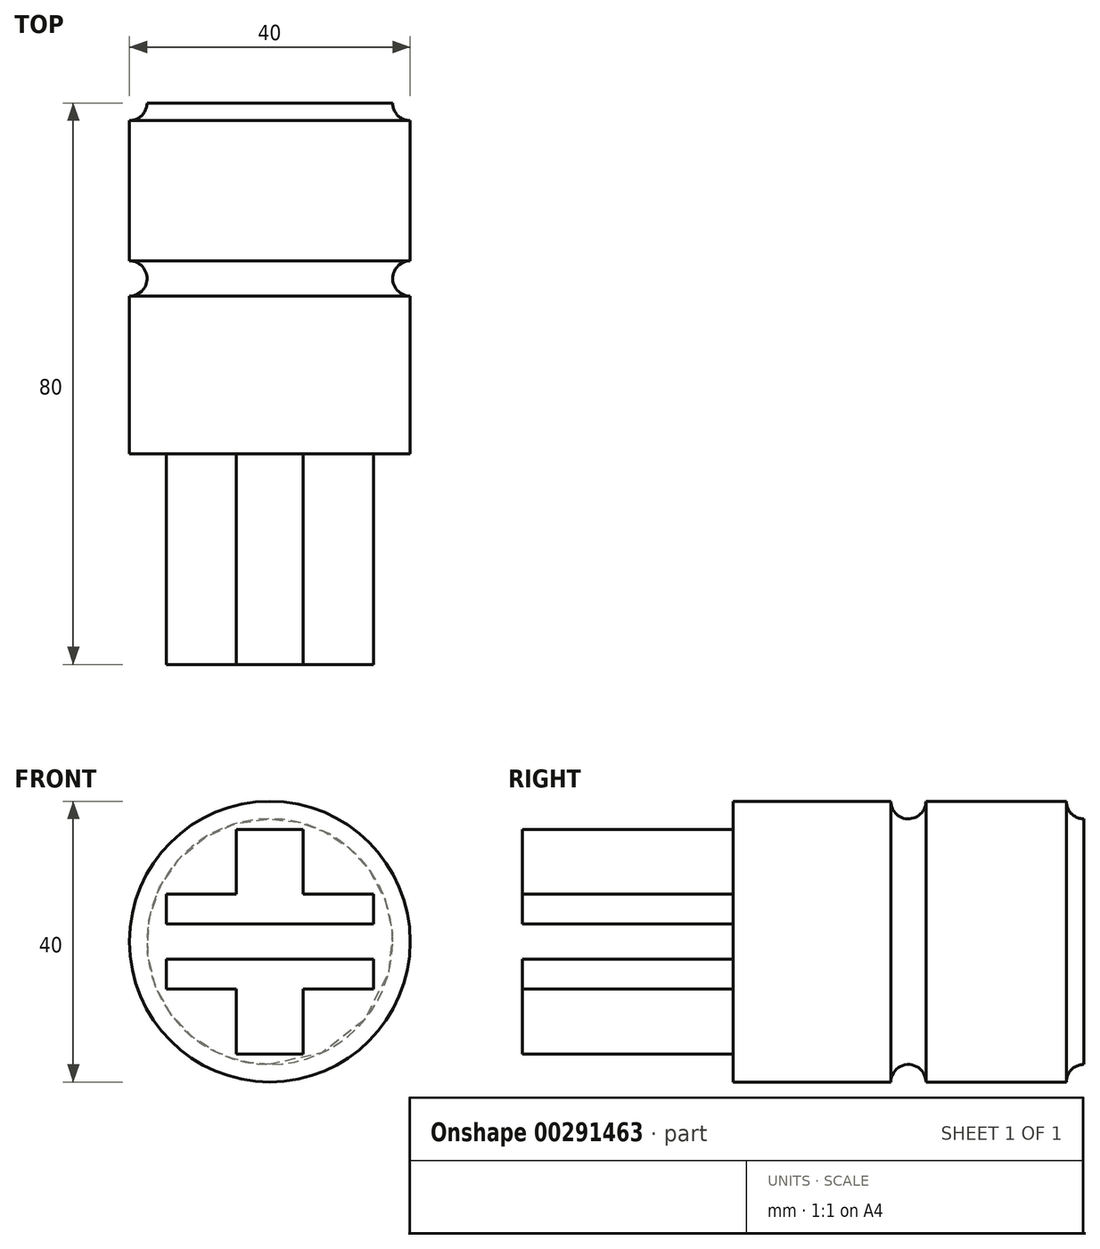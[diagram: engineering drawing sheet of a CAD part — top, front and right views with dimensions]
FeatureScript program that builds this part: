
annotation { "Feature Type Name" : "Feature", "Feature Type Description" : "" }
export const myFeature = defineFeature(function(context is Context, id is Id, definition is map)
    precondition{}
    {
        {
            var Q0;
            Q0=qCreatedBy(makeId("Front.planeOp"),FACE);
            var sketch = newSketch(context, id + "F0", { "sketchPlane" : qUnion([Q0])});
            skPoint(sketch, "E0.MirrorP", {"position": v(45.44, -3.17) * mm});
            skCircle(sketch, "E1", {"center": v(0, 0) * mm, "radius": 20 * mm});
            skLineSegment(sketch, "E2.left", {"start": v(20, -7.5) * mm, "end": v(20, 7.5) * mm});
            skLineSegment(sketch, "E2.right", {"start": v(-20, -7.5) * mm, "end": v(-20, 7.5) * mm});
            skLineSegment(sketch, "E3.bottom", {"start": v(7.5, -20) * mm, "end": v(-7.5, -20) * mm});
            skLineSegment(sketch, "E3.top", {"start": v(7.5, 20) * mm, "end": v(-7.5, 20) * mm});
            skLineSegment(sketch, "E4", {"start": v(-1.5, 0) * mm, "end": v(52.37, 0) * mm, "construction": true});
            skLineSegment(sketch, "E5.0", {"start": v(-4.75, 16) * mm, "end": v(-0.25, 16) * mm});
            skLineSegment(sketch, "E5.1", {"start": v(-0.25, 2.5) * mm, "end": v(-14.75, 2.5) * mm});
            skLineSegment(sketch, "E5.2", {"start": v(-14.75, 2.5) * mm, "end": v(-14.75, 6.75) * mm});
            skLineSegment(sketch, "E5.3", {"start": v(-14.75, 6.75) * mm, "end": v(-4.75, 6.75) * mm});
            skLineSegment(sketch, "E5.4", {"start": v(-4.75, 6.75) * mm, "end": v(-4.75, 16) * mm});
            skLineSegment(sketch, "E6", {"start": v(-0.25, 16) * mm, "end": v(-0.25, 2.5) * mm});
            skLineSegment(sketch, "E7", {"start": v(-0.25, 17.07) * mm, "end": v(-0.25, -22.61) * mm, "construction": true});
            skLineSegment(sketch, "E8.MirrorCS", {"start": v(4.75, 16) * mm, "end": v(0.25, 16) * mm});
            skLineSegment(sketch, "E9.MirrorCS", {"start": v(4.75, 6.75) * mm, "end": v(4.75, 16) * mm});
            skLineSegment(sketch, "E10.MirrorCS", {"start": v(14.75, 6.75) * mm, "end": v(4.75, 6.75) * mm});
            skLineSegment(sketch, "E11.MirrorCS", {"start": v(14.75, 2.5) * mm, "end": v(14.75, 6.75) * mm});
            skLineSegment(sketch, "E12.MirrorCS", {"start": v(0.25, 2.5) * mm, "end": v(14.75, 2.5) * mm});
            skLineSegment(sketch, "E13.MirrorCS", {"start": v(4.75, -6.75) * mm, "end": v(4.75, -16) * mm});
            skLineSegment(sketch, "E14.MirrorCS", {"start": v(14.75, -2.5) * mm, "end": v(14.75, -6.75) * mm});
            skLineSegment(sketch, "E15.MirrorCS", {"start": v(14.75, -6.75) * mm, "end": v(4.75, -6.75) * mm});
            skLineSegment(sketch, "E16.MirrorCS", {"start": v(0.25, -2.5) * mm, "end": v(14.75, -2.5) * mm});
            skLineSegment(sketch, "E17.MirrorCS", {"start": v(4.75, -16) * mm, "end": v(0.25, -16) * mm});
            skLineSegment(sketch, "E18.MirrorCS", {"start": v(-4.75, -16) * mm, "end": v(-0.25, -16) * mm});
            skLineSegment(sketch, "E19.MirrorCS", {"start": v(-4.75, -6.75) * mm, "end": v(-4.75, -16) * mm});
            skLineSegment(sketch, "E20.MirrorCS", {"start": v(-14.75, -6.75) * mm, "end": v(-4.75, -6.75) * mm});
            skLineSegment(sketch, "E21.MirrorCS", {"start": v(-14.75, -2.5) * mm, "end": v(-14.75, -6.75) * mm});
            skLineSegment(sketch, "E22.MirrorCS", {"start": v(-0.25, -2.5) * mm, "end": v(-14.75, -2.5) * mm});
            skLineSegment(sketch, "E23", {"start": v(-14.75, -2.5) * mm, "end": v(-14.75, 2.5) * mm});
            skLineSegment(sketch, "E24", {"start": v(14.75, -2.5) * mm, "end": v(14.75, 2.5) * mm});
            skLineSegment(sketch, "E25", {"start": v(0.25, 16) * mm, "end": v(-0.25, 16) * mm});
            skLineSegment(sketch, "E26", {"start": v(-0.25, -2.5) * mm, "end": v(0.25, -2.5) * mm});
            skLineSegment(sketch, "E27", {"start": v(-0.25, 2.5) * mm, "end": v(0.25, 2.5) * mm});
            skLineSegment(sketch, "E28", {"start": v(-0.25, -16) * mm, "end": v(0.25, -16) * mm});
            skSolve(sketch);
        }
        {
            var Q0;
            Q0=makeQuery(id+"F0.imprint","IMPRINT",FACE,{"disambiguationData":[TD([[makeQuery(id+"F0.imprint","IMPRINT",EDGE,{"derivedFrom":sQuery(id+"F0.wireOp",EDGE,"E5.0")}),-1.0]])]});
            var Q1;
            Q1=makeQuery(id+"F0.imprint","IMPRINT",FACE,{"disambiguationData":[TD([[makeQuery(id+"F0.imprint","IMPRINT",EDGE,{"derivedFrom":sQuery(id+"F0.wireOp",EDGE,"E6")}),1.0]])]});
            var Q2;
            Q2=makeQuery(id+"F0.imprint","IMPRINT",FACE,{"disambiguationData":[TD([[makeQuery(id+"F0.imprint","IMPRINT",EDGE,{"derivedFrom":sQuery(id+"F0.wireOp",EDGE,"E13.MirrorCS")}),-1.0]])]});
            extrude(context, id + "F1", {"entities" : qUnion([Q0, Q1, Q2]), "depth" : 30 * mm});
        }
        {
            var Q0;
            Q0=makeQuery(id+"F0.imprint","IMPRINT",FACE,{"disambiguationData":[TD([[makeQuery(id+"F0.imprint","IMPRINT",EDGE,{"derivedFrom":sQuery(id+"F0.wireOp",EDGE,"E1")}),1.0]])]});
            var Q1;
            Q1=makeQuery(id+"F0.imprint","IMPRINT",FACE,{"disambiguationData":[TD([[makeQuery(id+"F0.imprint","IMPRINT",EDGE,{"derivedFrom":sQuery(id+"F0.wireOp",EDGE,"1b40c791-a763-44da-a63f-c3d8366a5112")}),1.0]])]});
            var Q2;
            Q2=makeQuery(id+"F0.imprint","IMPRINT",FACE,{"disambiguationData":[TD([[makeQuery(id+"F0.imprint","IMPRINT",EDGE,{"derivedFrom":sQuery(id+"F0.wireOp",EDGE,"eddcf6a5-0345-47d6-95e7-a406ba912691")}),-1.0]])]});
            var Q3;
            Q3=makeQuery(id+"F0.imprint","IMPRINT",FACE,{"disambiguationData":[TD([[makeQuery(id+"F0.imprint","IMPRINT",EDGE,{"derivedFrom":sQuery(id+"F0.wireOp",EDGE,"936e1079-b66b-456b-97d4-c419b22d0ff1.MirrorCS")}),-1.0]])]});
            var Q4;
            Q4=makeQuery(id+"F0.imprint","IMPRINT",FACE,{"disambiguationData":[TD([[makeQuery(id+"F0.imprint","IMPRINT",EDGE,{"derivedFrom":sQuery(id+"F0.wireOp",EDGE,"eddcf6a5-0345-47d6-95e7-a406ba912691")}),1.0]])]});
            var Q5;
            Q5=makeQuery(id+"F0.imprint","IMPRINT",FACE,{"disambiguationData":[TD([[makeQuery(id+"F0.imprint","IMPRINT",EDGE,{"derivedFrom":sQuery(id+"F0.wireOp",EDGE,"E5.1")}),1.0]])]});
            var Q6;
            Q6=makeQuery(id+"F0.imprint","IMPRINT",FACE,{"disambiguationData":[TD([[makeQuery(id+"F0.imprint","IMPRINT",EDGE,{"derivedFrom":sQuery(id+"F0.wireOp",EDGE,"E5.0")}),-1.0]])]});
            var Q7;
            Q7=makeQuery(id+"F0.imprint","IMPRINT",FACE,{"disambiguationData":[TD([[makeQuery(id+"F0.imprint","IMPRINT",EDGE,{"derivedFrom":sQuery(id+"F0.wireOp",EDGE,"E13.MirrorCS")}),-1.0]])]});
            var Q8;
            Q8=makeQuery(id+"F0.imprint","IMPRINT",FACE,{"disambiguationData":[TD([[makeQuery(id+"F0.imprint","IMPRINT",EDGE,{"derivedFrom":sQuery(id+"F0.wireOp",EDGE,"E6")}),1.0]])]});
            extrude(context, id + "F2", {"entities" : qUnion([Q0, Q1, Q2, Q3, Q4, Q5, Q6, Q7, Q8]), "operationType" : NewBodyOperationType.ADD, "oppositeDirection" : true, "depth" : 50 * mm});
        }
        {
            var Q0;
            Q0=qCreatedBy(makeId("Front.planeOp"),FACE);
            cPlane(context, id + "F3", {"entities" : qUnion([Q0]), "cplaneType" : CPlaneType.OFFSET, "offset" : 50 * mm, "oppositeDirection" : true, "width" : 150 * mm, "height" : 150 * mm});
        }
        {
            var Q0;
            Q0=qCreatedBy(makeId("Right.planeOp"),FACE);
            var sketch = newSketch(context, id + "F4", { "sketchPlane" : qUnion([Q0])});
            skLineSegment(sketch, "E29", {"start": v(0, 20) * mm, "end": v(100, 20) * mm});
            skLineSegment(sketch, "E30", {"start": v(100, -20) * mm, "end": v(0, -20) * mm});
            skCircle(sketch, "E31", {"center": v(50, 20) * mm, "radius": 2.5 * mm});
            skCircle(sketch, "E32.1.0.0", {"center": v(75, 20) * mm, "radius": 2.5 * mm});
            skLineSegment(sketch, "E32.direction1", {"start": v(50, 20) * mm, "end": v(75, 20) * mm, "construction": true});
            skCircle(sketch, "E33.MirrorC", {"center": v(25, 20) * mm, "radius": 2.5 * mm});
            skCircle(sketch, "E34.MirrorC", {"center": v(0, 20) * mm, "radius": 2 * mm});
            skLineSegment(sketch, "E35", {"start": v(0, 0) * mm, "end": v(80.78, 0) * mm, "construction": true});
            skCircle(sketch, "E36.MirrorC", {"center": v(100, 20) * mm, "radius": 2 * mm});
            skSolve(sketch);
        }
        {
            var Q0;
            Q0=makeQuery(id+"F4.imprint","IMPRINT",FACE,{"disambiguationData":[TD([[makeQuery(id+"F4.imprint","IMPRINT",EDGE,{"derivedFrom":sQuery(id+"F4.wireOp",EDGE,"E34.MirrorC")}),-1.0]])]});
            var Q1;
            {var subQ0=sQuery(id+"F4.wireOp",EDGE,"E33.MirrorC");var subQ1=sQuery(id+"F4.wireOp",EDGE,"E29");var subQ2=makeQuery(id+"F4.imprint","INTERSECT",VERTEX,{"disambiguationData":[OD(0.0)],"derivedFrom":[subQ1,subQ0]});Q1=makeQuery(id+"F4.imprint","IMPRINT",FACE,{"disambiguationData":[TD([[makeQuery(id+"F4.imprint","IMPRINT",EDGE,{"disambiguationData":[TD([[subQ2,-1.0]])],"derivedFrom":subQ1}),-1.0]])]});}
            var Q2;
            {var subQ0=sQuery(id+"F4.wireOp",EDGE,"E33.MirrorC");var subQ1=sQuery(id+"F4.wireOp",EDGE,"E29");var subQ2=makeQuery(id+"F4.imprint","INTERSECT",VERTEX,{"disambiguationData":[OD(0.0)],"derivedFrom":[subQ1,subQ0]});Q2=makeQuery(id+"F4.imprint","IMPRINT",FACE,{"disambiguationData":[TD([[makeQuery(id+"F4.imprint","IMPRINT",EDGE,{"disambiguationData":[TD([[subQ2,-1.0]])],"derivedFrom":subQ1}),1.0]])]});}
            var Q3;
            {var subQ0=sQuery(id+"F4.wireOp",EDGE,"E31");var subQ1=sQuery(id+"F4.wireOp",EDGE,"E29");var subQ2=makeQuery(id+"F4.imprint","INTERSECT",VERTEX,{"disambiguationData":[OD(0.0)],"derivedFrom":[subQ1,subQ0]});Q3=makeQuery(id+"F4.imprint","IMPRINT",FACE,{"disambiguationData":[TD([[makeQuery(id+"F4.imprint","IMPRINT",EDGE,{"disambiguationData":[TD([[subQ2,-1.0]])],"derivedFrom":subQ1}),-1.0]])]});}
            var Q4;
            {var subQ0=sQuery(id+"F4.wireOp",EDGE,"E31");var subQ1=sQuery(id+"F4.wireOp",EDGE,"E29");var subQ2=makeQuery(id+"F4.imprint","INTERSECT",VERTEX,{"disambiguationData":[OD(0.0)],"derivedFrom":[subQ1,subQ0]});Q4=makeQuery(id+"F4.imprint","IMPRINT",FACE,{"disambiguationData":[TD([[makeQuery(id+"F4.imprint","IMPRINT",EDGE,{"disambiguationData":[TD([[subQ2,-1.0]])],"derivedFrom":subQ1}),1.0]])]});}
            var Q5;
            {var subQ0=sQuery(id+"F4.wireOp",EDGE,"E32.1.0.0");var subQ1=sQuery(id+"F4.wireOp",EDGE,"E29");var subQ2=makeQuery(id+"F4.imprint","INTERSECT",VERTEX,{"disambiguationData":[OD(0.0)],"derivedFrom":[subQ1,subQ0]});Q5=makeQuery(id+"F4.imprint","IMPRINT",FACE,{"disambiguationData":[TD([[makeQuery(id+"F4.imprint","IMPRINT",EDGE,{"disambiguationData":[TD([[subQ2,-1.0]])],"derivedFrom":subQ1}),-1.0]])]});}
            var Q6;
            {var subQ0=sQuery(id+"F4.wireOp",EDGE,"E32.1.0.0");var subQ1=sQuery(id+"F4.wireOp",EDGE,"E29");var subQ2=makeQuery(id+"F4.imprint","INTERSECT",VERTEX,{"disambiguationData":[OD(0.0)],"derivedFrom":[subQ1,subQ0]});Q6=makeQuery(id+"F4.imprint","IMPRINT",FACE,{"disambiguationData":[TD([[makeQuery(id+"F4.imprint","IMPRINT",EDGE,{"disambiguationData":[TD([[subQ2,-1.0]])],"derivedFrom":subQ1}),1.0]])]});}
            var Q7;
            Q7=makeQuery(id+"F4.imprint","IMPRINT",FACE,{"disambiguationData":[TD([[makeQuery(id+"F4.imprint","IMPRINT",EDGE,{"derivedFrom":sQuery(id+"F4.wireOp",EDGE,"E36.MirrorC")}),1.0]])]});
            var Q8;
            Q8=sQuery(id+"F4.wireOp",EDGE,"E35");
            revolve(context, id + "F5", {"operationType" : NewBodyOperationType.REMOVE, "entities" : qUnion([Q0, Q1, Q2, Q3, Q4, Q5, Q6, Q7]), "axis" : qUnion([Q8]), "revolveType" : RevolveType.FULL});
        }
    });
